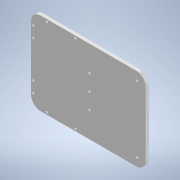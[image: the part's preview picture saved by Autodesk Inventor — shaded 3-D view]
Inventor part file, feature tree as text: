
AUTODESK INVENTOR PART (.ipt)
format: ipt  version: 2020 (Build 240168000, 168)  size: 134,144 bytes
history: native  units: mm
features: reference x5, other x3, sketch x2, extrude x1, hole x1
ambient origin geometry x8: Origin, YZ Plane, XZ Plane, XY Plane, X Axis, Y Axis, Z Axis, Center Point
bodies: Solid1 (feature_tree)
feature tree (12):
  extrude  "Extrusion1"  Depth=180.0mm
  hole  "Hole1"  [1 undecoded]
  sketch  "Sketch1"  dims[d0=130.0mm d1=180.0mm]
  sketch  "Sketch2"  dims[d2=15.0mm d3=15.0mm d4=5.0mm d5=0.0mm d6=3.4mm d7=6.0mm d8=6.3mm d9=2.0mm d10=90.0deg d11=8.0mm d12=20.594885mm]
  reference  "Reference1"
  reference  "Reference2"
  reference  "Reference3"
  reference  "Reference4"
  reference  "Reference5"
  other  "<userpath>\Desktop\KangKangBalancing\KangKang.iam"
  other  "KangKang.iam"
  other  "fleet:1"
note: 1 required parameter value undecoded (feature->parameter linkage not recoverable at this tier; creation-order binding heuristic only, values carry confidence <= 0.55)
